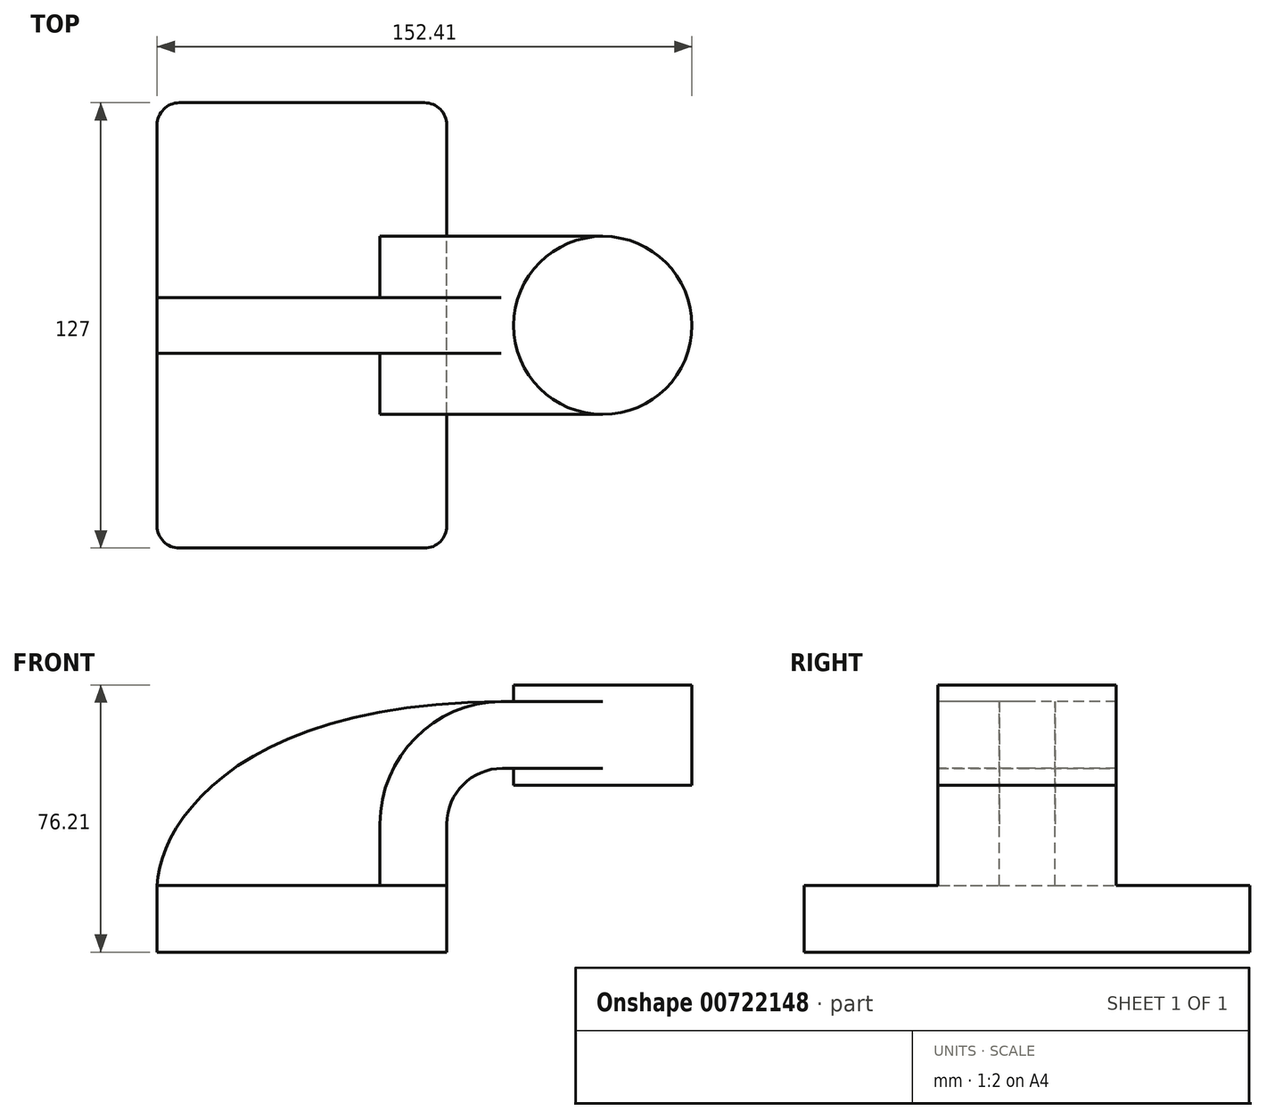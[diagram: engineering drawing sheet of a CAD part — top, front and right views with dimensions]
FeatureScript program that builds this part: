
annotation { "Feature Type Name" : "Feature", "Feature Type Description" : "" }
export const myFeature = defineFeature(function(context is Context, id is Id, definition is map)
    precondition{}
    {
        {
            var Q0;
            Q0=qCreatedBy(makeId("Front.planeOp"),FACE);
            var sketch = newSketch(context, id + "F0", { "sketchPlane" : qUnion([Q0])});
            skLineSegment(sketch, "E0.bottom", {"start": v(-41.28, 9.52) * mm, "end": v(41.28, 9.53) * mm});
            skLineSegment(sketch, "E0.top", {"start": v(-41.28, -9.53) * mm, "end": v(41.28, -9.53) * mm});
            skLineSegment(sketch, "E0.left", {"start": v(-41.28, 9.52) * mm, "end": v(-41.28, -9.53) * mm});
            skLineSegment(sketch, "E0.right", {"start": v(41.28, 9.53) * mm, "end": v(41.28, -9.52) * mm});
            skPoint(sketch, "E0.middle", {"position": v(0, 0) * mm});
            skLineSegment(sketch, "E1.bottom", {"start": v(111.12, 66.68) * mm, "end": v(60.32, 66.68) * mm});
            skLineSegment(sketch, "E1.top", {"start": v(111.12, 38.1) * mm, "end": v(60.32, 38.1) * mm});
            skLineSegment(sketch, "E1.left", {"start": v(111.12, 66.68) * mm, "end": v(111.12, 38.1) * mm});
            skLineSegment(sketch, "E1.right", {"start": v(60.32, 66.68) * mm, "end": v(60.32, 38.1) * mm});
            skPoint(sketch, "E1.middle", {"position": v(85.72, 52.39) * mm});
            skLineSegment(sketch, "E2", {"start": v(41.27, 9.53) * mm, "end": v(41.27, 27) * mm});
            skArc(sketch, "E3", {"start": v(41.27, 27) * mm, "mid": v(45.92, 38.23) * mm, "end": v(57.15, 42.88) * mm});
            skLineSegment(sketch, "E4", {"start": v(57.15, 42.88) * mm, "end": v(85.72, 42.88) * mm});
            skLineSegment(sketch, "E5.0", {"start": v(57.15, 61.93) * mm, "end": v(85.72, 61.93) * mm});
            skArc(sketch, "E5.1", {"start": v(22.22, 27) * mm, "mid": v(32.45, 51.7) * mm, "end": v(57.15, 61.93) * mm});
            skLineSegment(sketch, "E5.2", {"start": v(22.22, 9.53) * mm, "end": v(22.22, 27) * mm});
            skLineSegment(sketch, "E6", {"start": v(85.72, 38.1) * mm, "end": v(85.72, 66.68) * mm});
            skFitSpline(sketch, "E7", {"points": [v(-41.28, 9.52) * mm, v(57.15, 61.93) * mm], "startDerivative": vector(2.47, 53.26) * mm, "endDerivative": vector(227.57, 1.15) * mm});
            skSolve(sketch);
        }
        {
            var Q0;
            Q0=makeQuery(id+"F0.imprint","IMPRINT",FACE,{"disambiguationData":[TD([[makeQuery(id+"F0.imprint","IMPRINT",EDGE,{"derivedFrom":sQuery(id+"F0.wireOp",EDGE,"E0.top")}),1.0]])]});
            extrude(context, id + "F1", {"entities" : qUnion([Q0]), "endBound" : BoundingType.SYMMETRIC, "depth" : 127 * mm, "offsetDistance" : 25.4 * mm});
        }
        {
            var Q0;
            {var subQ1=sQuery(id+"F0.wireOp",EDGE,"E2");Q0=makeQuery(id+"F0.imprint","IMPRINT",FACE,{"disambiguationData":[TD([[makeQuery(id+"F0.imprint","IMPRINT",EDGE,{"derivedFrom":subQ1}),1.0]])]});}
            var Q1;
            {var subQ0=sQuery(id+"F0.wireOp",EDGE,"E5.0");var subQ1=sQuery(id+"F0.wireOp",EDGE,"E1.right");var subQ2=makeQuery(id+"F0.imprint","INTERSECT",VERTEX,{"derivedFrom":[subQ1,subQ0]});Q1=makeQuery(id+"F0.imprint","IMPRINT",FACE,{"disambiguationData":[TD([[makeQuery(id+"F0.imprint","IMPRINT",EDGE,{"disambiguationData":[TD([[subQ2,-1.0]])],"derivedFrom":subQ1}),1.0]])]});}
            extrude(context, id + "F2", {"entities" : qUnion([Q0, Q1]), "operationType" : NewBodyOperationType.ADD, "endBound" : BoundingType.SYMMETRIC, "depth" : 50.8 * mm, "offsetDistance" : 25.4 * mm});
        }
        {
            var Q0;
            {var subQ3=sQuery(id+"F0.wireOp",EDGE,"E5.2");Q0=makeQuery(id+"F0.imprint","IMPRINT",FACE,{"disambiguationData":[TD([[makeQuery(id+"F0.imprint","IMPRINT",EDGE,{"derivedFrom":subQ3}),1.0]])]});}
            extrude(context, id + "F3", {"entities" : qUnion([Q0]), "operationType" : NewBodyOperationType.ADD, "endBound" : BoundingType.SYMMETRIC, "depth" : 15.88 * mm, "offsetDistance" : 25.4 * mm});
        }
        {
            var Q0;
            {var subQ0=sQuery(id+"F0.wireOp",EDGE,"E1.left");Q0=makeQuery(id+"F0.imprint","IMPRINT",FACE,{"disambiguationData":[TD([[makeQuery(id+"F0.imprint","IMPRINT",EDGE,{"derivedFrom":subQ0}),-1.0]])]});}
            var Q1;
            Q1=sQuery(id+"F0.wireOp",EDGE,"E6");
            revolve(context, id + "F4", {"operationType" : NewBodyOperationType.ADD, "surfaceOperationType" : NewSurfaceOperationType.NEW, "entities" : qUnion([Q0]), "axis" : qUnion([Q1]), "revolveType" : RevolveType.FULL});
        }
        {
            var Q0;
            Q0=makeQuery(id+"F1.opExtrude","CAP_EDGE",EDGE,{"disambiguationData":[OSD([sQuery(id+"F0.wireOp",EDGE,"E0.left")])],"isStart":false});
            var Q1;
            Q1=makeQuery(id+"F1.opExtrude","CAP_EDGE",EDGE,{"disambiguationData":[OSD([sQuery(id+"F0.wireOp",EDGE,"E0.right")])],"isStart":false});
            var Q2;
            Q2=makeQuery(id+"F1.opExtrude","CAP_EDGE",EDGE,{"disambiguationData":[OSD([sQuery(id+"F0.wireOp",EDGE,"E0.right")])],"isStart":true});
            var Q3;
            Q3=makeQuery(id+"F1.opExtrude","CAP_EDGE",EDGE,{"disambiguationData":[OSD([sQuery(id+"F0.wireOp",EDGE,"E0.left")])],"isStart":true});
            fillet(context, id + "F5", {"entities" : qUnion([Q0, Q1, Q2, Q3]), "radius" : 6.35 * mm, "tangentPropagation" : true, "allowEdgeOverflow" : false});
        }
    });
